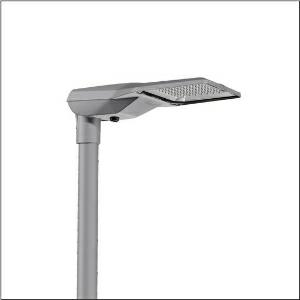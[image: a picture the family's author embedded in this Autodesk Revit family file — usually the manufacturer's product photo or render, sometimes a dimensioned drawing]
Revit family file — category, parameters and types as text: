
# Revit family: streetlight_sl_21_iq_midi___st1_0a_5xe3d31u08nb_218c
name_source: partatom
category: Lighting Fixtures
units: mm (PartAtom-declared; Revit-internal decimal feet)

## family parameters
Cut with Voids When Loaded = No
Host = Face
Light Source = No
Part Type = Normal
Room Calculation Point = No
Round Connector Dimension = Use Diameter
Shared = No

## types (1)
- --- (1 x LED, 21550 lm, 136.6 W, 3000K)
    Apparent Load = 137 VA
    CIE Flux Codes = 40 73 97 100 100
    Color Rendering = 70
    Color Temperature = 3000K
    Default Elevation = 1800 mm
    Description = Streetlight SL 21 iQ midi, mast luminaire, primary light control with lens, of PMMA, primary optical cover: cover, of toughened safety glass, transparent, light distribution: ST1.0a, light emission: direct distribution, primary light characteristic: asymmetric, installation type: post-top, side-entry, LED, High Power LED, rated luminous flux: 21.550lm, luminous efficacy: 158lm/W, light colour: 730, colour temperature: 3000K, control gear: iQ-Street Remote, D4i with power reduction, control: pre-setting: logarithmic dimming characteristic, Street-Remote, Auto-Match, Temp-Guard, Lumen-Switch, Night-Set, Smart-Wire, Light-Fading, Desk-Remote (wireless, voltage-free reading and setting of iQ features in the workshop via application-optimized NFC function/RFID function), optimised constant luminous flux control (CLO 2.0), mains connection: 230..240V, AC, 50/60Hz, start of lifetime: 137W, end of service life: 144W, reduction: 61W, luminaire housing, of diecast aluminium, powder-coated, Siteco® metallic grey (DB 702S), corrosivity category C5 mid according to DIN EN ISO 12944, please order mast flange separately, inclination adjustable: 0°, 5°, 10°, 15°, sealing non-destructively replaceable, multi-level sealing system, length: 644mm, width: 335mm, height: 110mm, mast flange for spigot size: 42mm (side-entry): 5XC10008XM4, 60/48mm (side-entry/post-top): 5XC10108XM2, 76/60mm (side-entry/post-top): 5XC10108XM1, mounting height: 4..8m, Smart Interface below, protection rating (complete): IP66, insulation class (complete): insulation class II (safety insulation), certification: CE, ENEC, ENEC+, VDE, impact resistance: IK10, permissible operating ambient temperature for outdoor applications: -40..+50°C, standard-compliant lighting for roads and squares, packaging unit: 1 piece

Light Distribution: ST1.0a
    Height = 111 mm
    Lamp = 1 x LED
    Lamp Light Flux = 21550 lm
    Lamp Power = 136.6 W
    Lamp count = 1
    Length = 644 mm
    Luminous efficacy = 158 lm/W
    Manufacturer = Siteco
    ModVariant = No
    Model = 5XE3D31U08NB
    Number of Poles = 1
    OnlyDefault = Yes
    Power Factor = 1
    Product Name = Streetlight SL 21 iQ midi | ST1.0a
    Product group = mast luminaire | pylon top
    ProductGroupID = 6100
    Protection Class = Protection class II
    Protection Degree = IP 66
    RLX_Detail_Level = 1
    RLX_Emergency_Light_Flux = 0 lm
    RLX_Emergency_Type = 0
    RLX_Emergency_Type_DB = No
    RlxData = <blob elided: 91193 chars, md5=c9271e3b>
    Socket = socket
    Standby Power = 0 W
    System Light Flux = 21550 lm
    System Power = 137 W
    Type Comments = factory setting: luminous flux: 100 % | dim-lin: 254 | 733 mA
    Type Image = l_1004300.jpg
    URL = http://relux.com
    VarID = @adj_135435
    Voltage = 0 V
    Weight = 0.00 kg
    Width = 336 mm

## geometry (parser evidence)
native form markers: Blend x4, Sweep x12
no freeform markers — native parametric forms only
